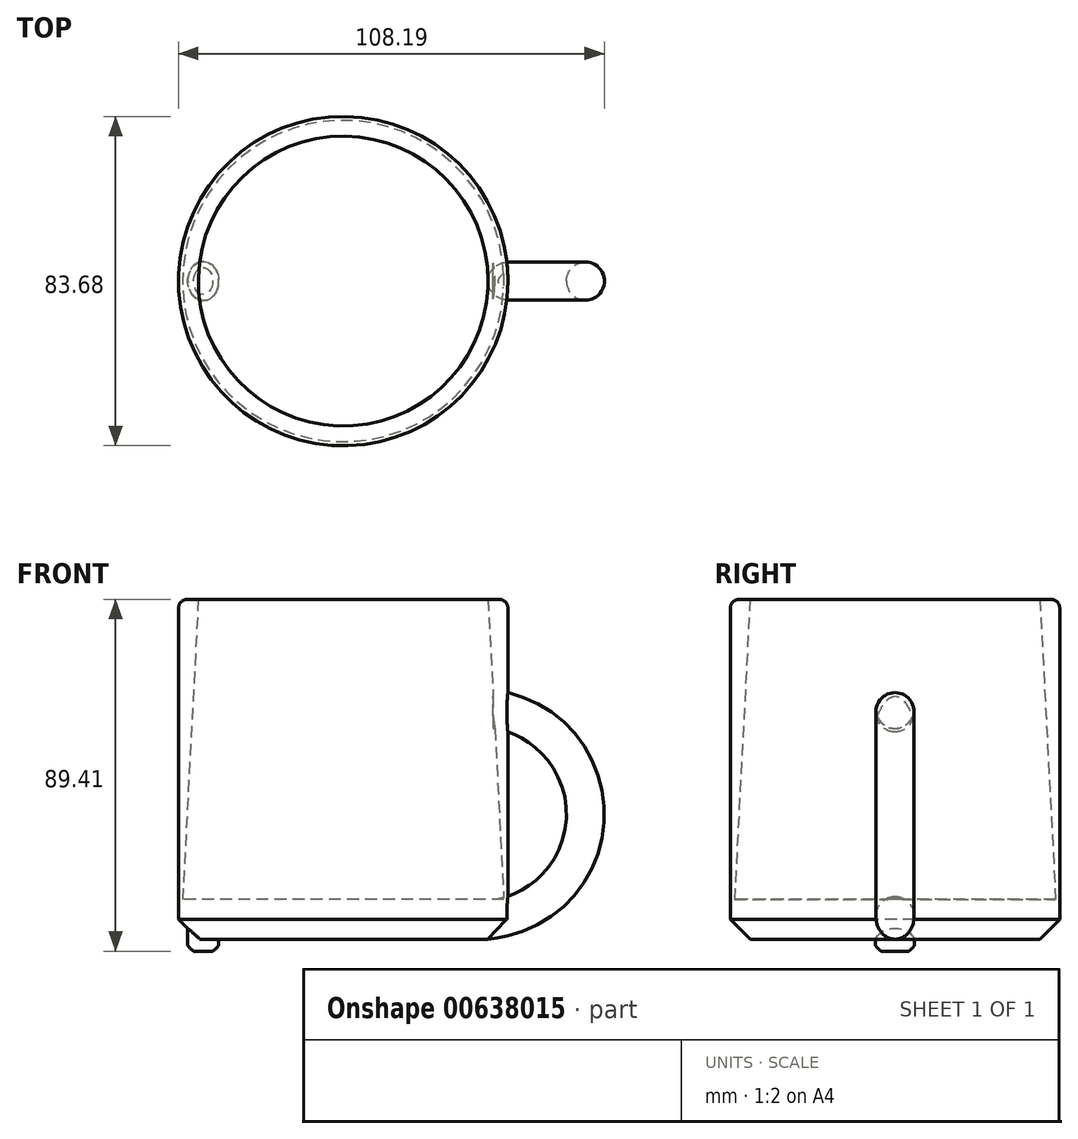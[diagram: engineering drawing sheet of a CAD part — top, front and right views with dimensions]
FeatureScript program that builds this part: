
annotation { "Feature Type Name" : "Feature", "Feature Type Description" : "" }
export const myFeature = defineFeature(function(context is Context, id is Id, definition is map)
    precondition{}
    {
        {
            var Q0;
            Q0=qCreatedBy(makeId("Top.planeOp"),FACE);
            var sketch = newSketch(context, id + "F0", { "sketchPlane" : qUnion([Q0])});
            skCircle(sketch, "E0", {"center": v(0, 0) * mm, "radius": 41.84 * mm});
            skSolve(sketch);
        }
        {
            var Q0;
            Q0 = qSketchRegion(id + "F0", true);
            extrude(context, id + "F1", {"entities" : qUnion([Q0]), "depth" : 86.36 * mm, "offsetDistance" : 25.4 * mm});
        }
        {
            var Q0;
            Q0=makeQuery(id+"F1.opExtrude","CAP_FACE",FACE,{"disambiguationData":[OSD([sQuery(id+"F0.wireOp",EDGE,"E0")])],"isStart":false});
            var sketch = newSketch(context, id + "F2", { "sketchPlane" : qUnion([Q0])});
            skCircle(sketch, "E1", {"center": v(0, 0) * mm, "radius": 36.8 * mm});
            skSolve(sketch);
        }
        {
            var Q0;
            Q0 = qSketchRegion(id + "F2", true);
            extrude(context, id + "F3", {"entities" : qUnion([Q0]), "operationType" : NewBodyOperationType.REMOVE, "oppositeDirection" : true, "depth" : 76.2 * mm, "offsetDistance" : 25.4 * mm, "hasDraft" : true, "draftAngle" : 3 * degree});
        }
        {
            var Q0;
            Q0=qCreatedBy(makeId("Front.planeOp"),FACE);
            var sketch = newSketch(context, id + "F4", { "sketchPlane" : qUnion([Q0])});
            skLineSegment(sketch, "E2", {"start": v(38.1, 58.42) * mm, "end": v(12.7, 58.42) * mm});
            skLineSegment(sketch, "E3", {"start": v(0, 31.75) * mm, "end": v(14.1, 31.75) * mm});
            skLineSegment(sketch, "E4.MirrorCS", {"start": v(38.1, 5.08) * mm, "end": v(12.7, 5.08) * mm});
            skArc(sketch, "E5", {"start": v(38.1, 5.08) * mm, "mid": v(61.53, 31.75) * mm, "end": v(38.1, 58.42) * mm});
            skSolve(sketch);
        }
        {
            var Q0;
            Q0=qCreatedBy(makeId("Right.planeOp"),FACE);
            var Q1;
            Q1=sQuery(id+"F4.wireOp",VERTEX,"E5.end");
            cPlane(context, id + "F5", {"entities" : qUnion([Q0, Q1]), "cplaneType" : CPlaneType.PLANE_POINT, "offset" : 25.4 * mm, "width" : 152.4 * mm, "height" : 152.4 * mm});
        }
        {
            var Q0;
            Q0=qCreatedBy(id+"F5.planeOp",FACE);
            var sketch = newSketch(context, id + "F6", { "sketchPlane" : qUnion([Q0])});
            skCircle(sketch, "E6", {"center": v(0, 58.42) * mm, "radius": 4.86 * mm});
            skSolve(sketch);
        }
        {
            var Q0;
            Q0 = qSketchRegion(id + "F6", true);
            var Q1;
            Q1=sQuery(id+"F4.wireOp",EDGE,"E5");
            sweep(context, id + "F7", {"operationType" : NewBodyOperationType.ADD, "profiles" : qUnion([Q0]), "path" : qUnion([Q1])});
        }
        {
            var Q0;
            Q0=makeQuery(id+"F1.opExtrude","CAP_EDGE",EDGE,{"disambiguationData":[OSD([sQuery(id+"F0.wireOp",EDGE,"E0")])],"isStart":false});
            var Q1;
            Q1=makeQuery(id+"F3.boolean.opBoolean","COPY",EDGE,{"derivedFrom":makeQuery(id+"F3.opExtrude","CAP_EDGE",EDGE,{"disambiguationData":[OSD([sQuery(id+"F2.wireOp",EDGE,"E1")])],"isStart":true})});
            fillet(context, id + "F8", {"entities" : qUnion([Q0, Q1]), "radius" : 2.3 * mm, "tangentPropagation" : true, "allowEdgeOverflow" : false});
        }
        {
            var Q0;
            Q0=makeQuery(id+"F1.opExtrude","CAP_FACE",FACE,{"disambiguationData":[OSD([sQuery(id+"F0.wireOp",EDGE,"E0")])],"isStart":true});
            var sketch = newSketch(context, id + "F9", { "sketchPlane" : qUnion([Q0])});
            skEllipse(sketch, "E7", {"center": v(-35.56, 0) * mm, "majorRadius": 5 * mm, "minorRadius": 3.94 * mm, "majorAxis": v(0, 1)});
            skSolve(sketch);
        }
        {
            var Q0;
            Q0=makeQuery(id+"F9.imprint","IMPRINT",FACE,{"disambiguationData":[TD([[makeQuery(id+"F9.imprint","IMPRINT",EDGE,{"derivedFrom":sQuery(id+"F9.wireOp",EDGE,"E7")}),1.0]])]});
            var Q1;
            Q1=sQuery(id+"F9.wireOp",EDGE,"E7");
            extrude(context, id + "F10", {"entities" : qUnion([Q0]), "operationType" : NewBodyOperationType.ADD, "surfaceEntities" : qUnion([Q1]), "depth" : 3.05 * mm, "offsetDistance" : 25.4 * mm});
        }
        {
            var Q0;
            Q0=makeQuery(id+"F10.opExtrude","CAP_FACE",FACE,{"disambiguationData":[OSD([sQuery(id+"F9.wireOp",EDGE,"E7")])],"isStart":false});
            fillet(context, id + "F11", {"entities" : qUnion([Q0]), "radius" : 1.52 * mm, "tangentPropagation" : true, "rho" : 0.1, "crossSection" : FilletCrossSection.CONIC, "allowEdgeOverflow" : false});
        }
        {
            var Q0;
            Q0=qCreatedBy(makeId("Right.planeOp"),FACE);
            var sketch = newSketch(context, id + "F12", { "sketchPlane" : qUnion([Q0])});
            skLineSegment(sketch, "E8", {"start": v(0, 0) * mm, "end": v(0, 55.56) * mm});
            skSolve(sketch);
        }
        {
            var Q0;
            Q0=makeQuery(id+"F1.opExtrude","CAP_EDGE",EDGE,{"disambiguationData":[OSD([sQuery(id+"F0.wireOp",EDGE,"E0")])],"isStart":true});
            chamfer(context, id + "F13", {"entities" : qUnion([Q0]), "width" : 5.08 * mm, "tangentPropagation" : true});
        }
    });
